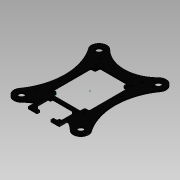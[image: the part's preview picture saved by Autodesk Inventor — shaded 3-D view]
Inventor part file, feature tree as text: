
AUTODESK INVENTOR PART (.ipt)
format: ipt  version: 2015 SP1 (Build 190203100, 203)  size: 549,888 bytes
history: native  units: mm
features: sketch x14, extrude x8, reference x2, projected_geometry x2
ambient origin geometry x8: Origin, YZ Plane, XZ Plane, XY Plane, X Axis, Y Axis, Z Axis, Center Point
bodies: Body1 (feature_tree)
feature tree (26):
  extrude  "Extrusion6"  Depth=9.0mm
  sketch  "Sketch5"  dims[d43=9.0mm d46=2.5mm]
  sketch  "Sketch7"  dims[d86=12.004481mm d87=6.00224mm]
  extrude  "Extrusion11"  Depth=2.5mm
  extrude  "Extrusion12"  Depth=6.00224mm
  sketch  "Sketch12"  dims[d95=5.821895mm d97=68.48mm]
  extrude  "Extrusion16"  Depth=69.254481mm
  extrude  "Extrusion17"  Depth=5.821895mm
  sketch  "Sketch16"  dims[d102=10.0mm]
  extrude  "Extrusion18"  Depth=68.48mm
  extrude  "Extrusion19"  Depth=9.0mm
  sketch  "Sketch18"  dims[d103=9.0mm]
  extrude  "Extrusion20"  Depth=2.5mm
  sketch  "Sketch20"  dims[d112=90.0deg]
  sketch  "Sketch21"  dims[d113=3.5mm]
  sketch  "Sketch22"  dims[d114=5.0mm d116=3.5mm d117=5.0mm d119=3.5mm d120=5.0mm d121=5.0mm d122=3.5mm d123=5.0mm d124=5.0mm d126=10.0mm d133=1.0mm d135=3.0mm d136=0.0mm d137=1.0mm d138=3.5mm d139=3.5mm d140=3.5mm d141=3.5mm d142=1.0mm d143=3.5mm d144=3.5mm d145=3.5mm d146=1.0mm d147=90.0deg d150=4.0mm d154=70.0mm d155=4.0mm d163=79.21229mm d164=117.809047mm d165=146.323167mm d166=3.5mm d167=0.0mm d170=146.323246mm d171=117.849958mm d172=3.0mm d173=0.0mm d181=146.323246mm d182=117.849958mm d183=3.5mm d186=40.0mm d187=37.5mm d190=90.0deg d194=10.0mm d195=0.0mm d198=43.0mm d199=85.0mm d200=43.0mm d201=85.0mm d202=10.0mm d203=0.0mm d204=3.0mm d205=0.0mm d206=0.0mm d207=0.0mm d208=30.222147mm d209=8.37276mm d210=26.980433mm d211=0.34724mm d212=3.0mm d213=0.0mm]
  sketch  "Sketch1"  dims[d26=29.0mm d42=9.0mm]
  sketch  "Sketch8"  dims[d88=6.00224mm d92=69.254481mm]
  sketch  "Sketch10"  dims[d93=27.79742mm d94=5.821895mm]
  sketch  "Sketch14"  dims[d98=51.000004mm d99=9.0mm]
  sketch  "Sketch15"  dims[d100=8.486696mm d101=2.5mm]
  reference  "Reference5"
  reference  "Reference6"
  sketch  "Sketch19"  dims[d104=8.486696mm]
  projected_geometry  "Projected Loop2"
  projected_geometry  "Projected Loop3"
